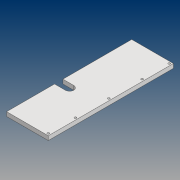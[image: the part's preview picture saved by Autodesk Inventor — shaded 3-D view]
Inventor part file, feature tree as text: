
AUTODESK INVENTOR PART (.ipt)
format: ipt  version: 2021 (Build 250183000, 183)  size: 105,472 bytes
history: native  units: mm
features: other x4, sketch x3, extrude x2, reference x2, hole x1
ambient origin geometry x8: Origin, YZ Plane, XZ Plane, XY Plane, X Axis, Y Axis, Z Axis, Center Point
bodies: Solid1 (feature_tree)
feature tree (12):
  extrude  "Extrusion1"  Depth=100.0mm
  extrude  "Extrusion2"  Depth=20.0mm
  hole  "Hole1"  [1 undecoded]
  sketch  "Sketch1"  dims[d0=300.0mm d1=100.0mm]
  sketch  "Sketch2"  dims[d2=10.0mm d3=0.0mm d4=20.0mm]
  reference  "Reference1"
  reference  "Reference2"
  sketch  "Sketch3"  dims[d5=10.0mm d6=0.0mm d7=5.0mm d8=5.0mm d9=80.0mm d10=5.0mm d11=6.0mm d12=4.0mm d13=2.0mm d14=90.0deg d15=8.0mm d16=20.594885mm]
  other  "0001_ASS_Ban_lap_ghep_01.iam"
  other  "000ASS_Bo_banh_xe_04:1"
  other  "02_Truc_02:1"
  other  "06_Tam_de_01:1"
note: 1 required parameter value undecoded (feature->parameter linkage not recoverable at this tier; creation-order binding heuristic only, values carry confidence <= 0.55)
